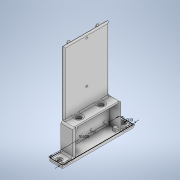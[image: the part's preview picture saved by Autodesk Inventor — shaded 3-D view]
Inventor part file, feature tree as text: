
AUTODESK INVENTOR PART (.ipt)
format: ipt  version: 2020 (Build 240168000, 168)  size: 503,296 bytes
history: native  units: in
note: dims shown in document units (in); Inventor stores cm internally (conversion verified against a paired STEP export)
features: sketch x14, extrude x9, hole x6, fillet x4, projected_geometry x2
ambient origin geometry x8: Origin, YZ Plane, XZ Plane, XY Plane, X Axis, Y Axis, Z Axis, Center Point
bodies: Solid1 (feature_tree)
feature tree (35):
  sketch  "Sketch1"  dims[d0=1.0in d1=5.5in]
  extrude  "Extrusion1"  Depth=1.0in
  hole  "Hole1"  [1 undecoded]
  extrude  "Extrusion2"  Depth=1.0in
  extrude  "Extrusion3"  Depth=3.5in
  extrude  "Extrusion4"  Depth=1.0in
  hole  "Hole2"  [1 undecoded]
  hole  "Hole3"  [1 undecoded]
  extrude  "Extrusion6"  Depth=0.75in TaperAngle=0.0deg
  extrude  "Extrusion7"  Depth=0.875in
  extrude  "Extrusion8"  Depth=1.025in
  hole  "Hole4"  [1 undecoded]
  hole  "Hole5"  [1 undecoded]
  fillet  "Fillet1"  Radius=0.175in
  fillet  "Fillet2"  Radius=0.175in
  extrude  "Extrusion9"  Depth=0.1in
  hole  "Hole6"  [1 undecoded]
  extrude  "Extrusion10"  Depth=0.1in
  fillet  "Fillet3"  Radius=0.25in
  fillet  "Fillet4"  Radius=1.225in
  sketch  "Sketch2"  dims[d2=0.25in d3=0.25in]
  sketch  "Sketch3"  dims[d4=0.25in d5=0.0in]
  sketch  "Sketch4"  dims[d6=0.281in d7=0.75in d8=0.438in d9=0.0625in d10=0.5635in d11=0.25in d12=0.0in d13=1.0in]
  sketch  "Sketch5"  dims[d14=0.125in d15=3.5in]
  projected_geometry  "Projected Loop1"
  sketch  "Sketch6"  dims[d16=1.0in d17=0.125in]
  projected_geometry  "Projected Loop2"
  sketch  "Sketch8"  dims[d18=1.0in d19=0.125in]
  sketch  "Sketch9"  dims[d20=2.0in d21=0.0in d22=3.5in]
  sketch  "Sketch10"  dims[d23=0.125in d24=0.75in d25=0.0in]
  sketch  "Sketch11"  dims[d26=0.9375in d27=0.875in]
  sketch  "Sketch12"  dims[d28=1.75in d29=1.025in]
  sketch  "Sketch13"  dims[d30=1.125in d31=1.025in]
  sketch  "Sketch14"  dims[d32=1.125in d33=0.175in d34=0.175in d35=0.175in]
  sketch  "Sketch15"  dims[d36=0.175in d37=0.175in d38=0.175in d39=0.175in d40=0.25in d41=0.0in d42=0.07in d43=0.75in d44=0.438in d45=0.25in d46=0.5635in d47=0.375in d48=0.0in d49=1.225in d50=1.325in d51=1.225in d52=1.325in d53=0.425in d54=0.425in d55=0.4in d56=0.75in d57=0.438in d58=0.25in d59=0.5635in d60=0.375in d61=0.0in d66=0.125in d67=0.125in d68=0.125in d69=0.125in d70=0.325in d71=0.25in d72=0.0in d73=0.25in d74=0.25in d75=0.25in d76=0.25in d77=0.25in d78=0.25in d79=0.0in d80=0.25in d81=0.125in d82=0.25in d83=0.25in d84=0.25in d85=0.0in d86=0.125in d87=0.125in d88=0.125in d89=0.089in d90=0.75in d91=0.438in d92=0.25in d93=0.5635in d94=0.375in d95=0.0in d96=0.125in d97=0.125in d98=0.125in d99=0.125in d100=0.125in d101=0.125in d102=0.125in d103=0.089in d104=0.75in d105=0.438in d106=0.25in d107=0.5635in d108=0.25in d109=0.0in d110=0.125in d111=0.125in d112=0.125in d113=3.5in d114=5.0in d115=0.0in d116=0.25in d117=3.25in d118=180.0deg d119=0.136in d120=0.75in d121=0.119in d122=0.112in d123=0.5635in d124=0.25in d125=0.0in d126=0.5in d127=0.5in d128=0.25in d129=0.25in d130=7.0in d131=0.25in d132=0.0in d133=0.1in d134=0.1in d62=0.5in d63=0.0344in d64=0.5in d65=0.0344in]
note: 6 required parameter values undecoded (feature->parameter linkage not recoverable at this tier; creation-order binding heuristic only, values carry confidence <= 0.55)
